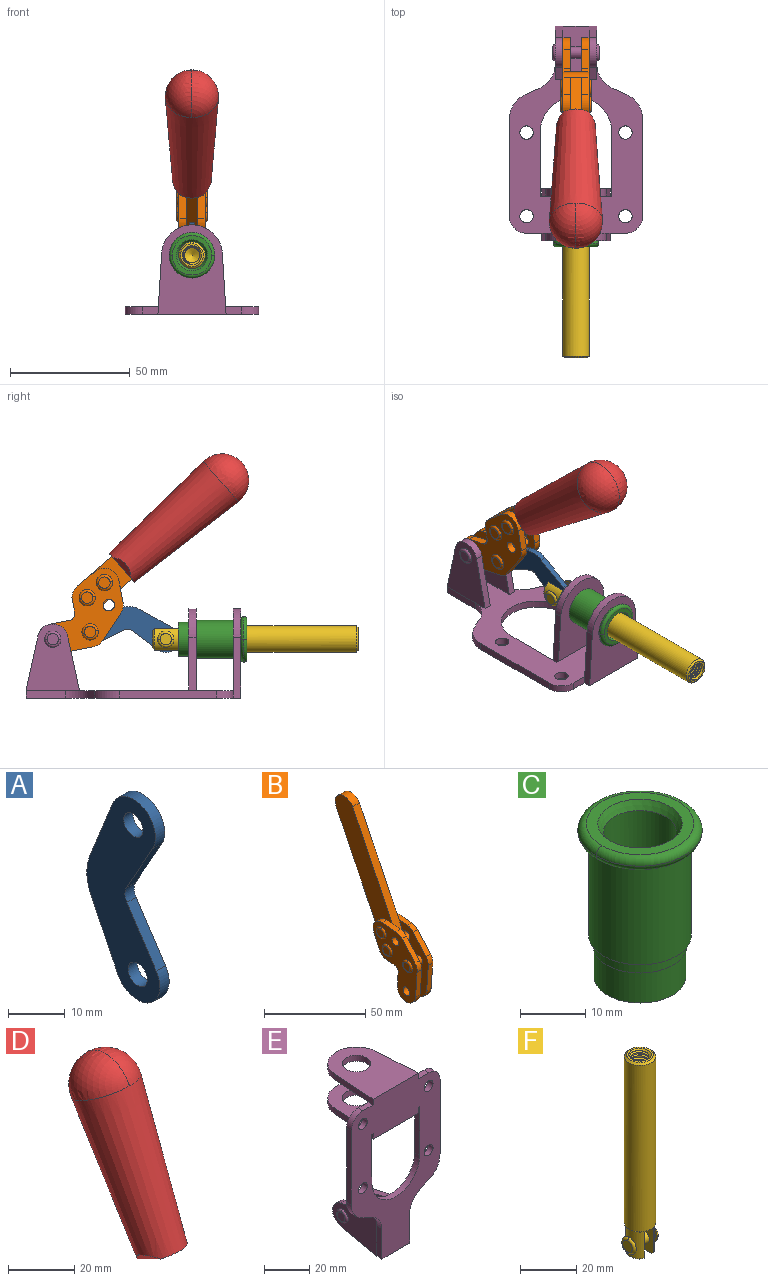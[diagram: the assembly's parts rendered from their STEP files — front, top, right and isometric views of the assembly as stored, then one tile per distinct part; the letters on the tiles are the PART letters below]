
ASSEMBLY  parts=6 mates=6
PART A: 12 faces, bbox 2.3x18.2x42.8 mm
  f0: cylinder r=2.4mm len=4.8mm, axis (1,0,0), area 34.9mm2, adj f4,f11
  f1: cylinder r=10.41mm len=8.47mm, axis (1,0,0), area 20.2mm2, adj f4,f9,f10,f11
  f2: cylinder r=3.05mm len=3.16mm, axis (1,0,0), area 7.7mm2, adj f4,f6,f7,f11
  f3: cylinder r=2.4mm len=4.8mm, axis (1,0,0), area 34.9mm2, adj f4,f11
  f4: plane 42.81x18.23mm, normal (-1,0,0), area 414.1mm2, adj f0,f1,f2,f3,f5,f6,f7,f8
  f5: cylinder r=5.54mm len=10.67mm, axis (1,0,0), area 41.8mm2, adj f4,f6,f10,f11
  f6: plane 11.66x6.53mm, normal (0,-0.87,-0.49), area 30.9mm2, adj f2,f4,f5,f11
  f7: plane 11.17x7.33mm, normal (0,-0.84,0.55), area 30.9mm2, adj f2,f4,f8,f11
  f8: cylinder r=5.54mm len=10.51mm, axis (1,0,0), area 41.8mm2, adj f4,f7,f9,f11
  f9: plane 13.67x6.67mm, normal (0,0.9,-0.44), area 35.1mm2, adj f1,f4,f8,f11
  f10: plane 14.1x5.7mm, normal (0,0.93,0.37), area 35.1mm2, adj f1,f4,f5,f11
  f11: plane 42.81x18.23mm, normal (1,0,0), area 414.1mm2, adj f0,f1,f2,f3,f5,f6,f7,f8
PART B: 59 faces, bbox 12.9x60.2x99.6 mm
  f0: torus R=2.39mm, axis (-1,0,0), area 14.9mm2, adj f20,f43,f51
  f1: torus R=2.39mm, axis (-1,0,0), area 14.9mm2, adj f19,f42,f51
  f2: torus R=2.39mm, axis (-1,0,0), area 14.9mm2, adj f18,f35,f51
  f3: torus R=2.39mm, axis (-1,0,0), area 14.9mm2, adj f14,f17,f23
  f4: torus R=2.39mm, axis (-1,0,0), area 14.9mm2, adj f13,f16,f23
  f5: torus R=2.39mm, axis (-1,0,0), area 14.9mm2, adj f12,f15,f23
  f6: cylinder r=2.39mm len=4.78mm, axis (1,0,0), area 46.5mm2, adj f48,f50,f51
  f7: cylinder r=2.39mm len=4.78mm, axis (1,0,0), area 46.5mm2, adj f50,f51
  f8: cylinder r=6.35mm len=12.68mm, axis (1,0,0), area 61.8mm2, adj f38,f39,f50,f51
  f9: cylinder r=2.39mm len=4.78mm, axis (-1,0,0), area 70.5mm2, adj f46,f50
  f10: cylinder r=2.39mm len=4.78mm, axis (-1,0,0), area 46.5mm2, adj f23,f45,f46
  f11: cylinder r=2.39mm len=4.78mm, axis (-1,0,0), area 46.5mm2, adj f23,f46
  f12: plane 4.78x4.78mm, normal (1,0,0), area 17.9mm2, adj f5,f15
  f13: plane 4.78x4.78mm, normal (1,0,0), area 17.9mm2, adj f4,f16
  f14: plane 4.78x4.78mm, normal (1,0,0), area 17.9mm2, adj f3,f17
  f15: torus R=2.39mm, axis (-1,0,0), area 14.9mm2, adj f5,f12,f23
  f16: torus R=2.39mm, axis (-1,0,0), area 14.9mm2, adj f4,f13,f23
  f17: torus R=2.39mm, axis (-1,0,0), area 14.9mm2, adj f3,f14,f23
  f18: plane 4.78x4.78mm, normal (-1,0,0), area 17.9mm2, adj f2,f35
  f19: plane 4.78x4.78mm, normal (-1,0,0), area 17.9mm2, adj f1,f42
  f20: plane 4.78x4.78mm, normal (-1,0,0), area 17.9mm2, adj f0,f43
  f21: plane 2.26x0.2mm, normal (1,0,0), area 0.2mm2, adj f31,f44
  f22: plane 2.26x0.2mm, normal (-1,0,0), area 0.2mm2, adj f41,f44
  f23: plane 39.37x30.77mm, normal (1,0,0), area 565.5mm2, adj f3,f4,f5,f10,f11,f15,f16,f17
  f24: cylinder r=6.1mm len=4.15mm, axis (-1,0,0), area 14.7mm2, adj f23,f25,f32,f46
  f25: plane 10.25x9.01mm, normal (0,-0.75,0.66), area 42.3mm2, adj f23,f24,f26,f46
  f26: cylinder r=6.35mm len=4.64mm, axis (-1,0,0), area 15.6mm2, adj f23,f25,f27,f46
  f27: plane 15.84x3.1mm, normal (0,-1,-0.07), area 49.2mm2, adj f23,f26,f28,f46
  f28: cylinder r=6.35mm len=12.68mm, axis (-1,0,0), area 61.8mm2, adj f23,f27,f29,f46
  f29: plane 8.11x3.1mm, normal (0,1,0.07), area 25.2mm2, adj f23,f28,f30,f46
  f30: cylinder r=3.05mm len=3.25mm, axis (-1,0,0), area 14.8mm2, adj f23,f29,f31,f46
  f31: plane 5.99x3.1mm, normal (0,0.07,-1), area 18.6mm2, adj f21,f23,f30,f44,f46
  f32: plane 9.5x3.1mm, normal (0,-0.07,1), area 29.5mm2, adj f23,f24,f33,f46,f47
  f33: cylinder r=6.1mm len=8.63mm, axis (-1,0,0), area 39.1mm2, adj f23,f32,f34,f47
  f34: plane 8.65x3.96mm, normal (0,0.91,-0.42), area 29.5mm2, adj f23,f33,f44,f47
  f35: torus R=2.39mm, axis (-1,0,0), area 14.9mm2, adj f2,f18,f51
  f36: plane 10.25x9.01mm, normal (0,-0.75,0.66), area 42.3mm2, adj f37,f49,f50,f51
  f37: cylinder r=6.35mm len=4.64mm, axis (1,0,0), area 15.6mm2, adj f36,f38,f50,f51
  f38: plane 15.84x3.1mm, normal (0,-1,-0.07), area 49.2mm2, adj f8,f37,f50,f51
  f39: plane 8.11x3.1mm, normal (0,1,0.07), area 25.2mm2, adj f8,f40,f50,f51
  f40: cylinder r=3.05mm len=3.25mm, axis (1,0,0), area 14.8mm2, adj f39,f41,f50,f51
  f41: plane 5.99x3.1mm, normal (0,0.07,-1), area 18.6mm2, adj f22,f40,f44,f50,f51
  f42: torus R=2.39mm, axis (-1,0,0), area 14.9mm2, adj f1,f19,f51
  f43: torus R=2.39mm, axis (-1,0,0), area 14.9mm2, adj f0,f20,f51
  f44: cylinder r=6.35mm len=12.12mm, axis (-1,0,0), area 128.9mm2, adj f21,f22,f23,f31,f34,f41,f46,f47
  f45: plane 2.65x1.35mm, normal (1,0,0), area 1mm2, adj f10,f55
  f46: plane 39.08x20.42mm, normal (-1,0,0), area 412.5mm2, adj f9,f10,f11,f24,f25,f26,f27,f28
  f47: plane 77.62x39.82mm, normal (1,0,0), area 850mm2, adj f32,f33,f34,f44,f53,f54,f55
  f48: plane 2.65x1.35mm, normal (-1,0,0), area 1mm2, adj f6,f55
  f49: cylinder r=6.1mm len=4.15mm, axis (1,0,0), area 14.7mm2, adj f36,f50,f51,f56
  f50: plane 39.08x20.42mm, normal (1,0,0), area 412.5mm2, adj f6,f7,f8,f9,f36,f37,f38,f39
  f51: plane 39.37x30.77mm, normal (-1,0,0), area 565.5mm2, adj f0,f1,f2,f6,f7,f8,f35,f36
  f52: plane 8.65x3.96mm, normal (0,0.91,-0.42), area 29.5mm2, adj f44,f51,f57,f58
  f53: plane 68.49x33.4mm, normal (0,0.9,-0.44), area 358.1mm2, adj f44,f47,f54,f58
  f54: cylinder r=6.35mm len=12.06mm, axis (1,0,0), area 93.7mm2, adj f47,f53,f55,f58
  f55: plane 68.49x33.4mm, normal (0,-0.9,0.44), area 358.1mm2, adj f44,f45,f46,f47,f48,f50,f54,f58
  f56: plane 9.5x3.1mm, normal (0,-0.07,1), area 29.5mm2, adj f49,f50,f51,f57,f58
  f57: cylinder r=6.1mm len=8.63mm, axis (1,0,0), area 39.1mm2, adj f51,f52,f56,f58
  f58: plane 77.62x39.82mm, normal (-1,0,0), area 850mm2, adj f44,f52,f53,f54,f55,f56,f57
PART C: 15 faces, bbox 20.6x20.6x28.7 mm
  f0: torus R=8.26mm, axis (0,0,1), area 56.8mm2, adj f1,f10,f12
  f1: torus R=8.26mm, axis (0,0,1), area 56.8mm2, adj f0,f6,f13
  f2: cylinder r=5.59mm len=25.91mm, axis (0,0,1), area 909.6mm2, adj f3,f4
  f3: cone r=6.86mm half-angle=45deg, axis (0,0,-1), area 70.2mm2, adj f2,f14
  f4: cone r=6.47mm half-angle=30deg, axis (0,0,1), area 66.7mm2, adj f2,f13
  f5: cylinder r=7.04mm len=14.07mm, axis (0,0,1), area 252.6mm2, adj f11,f14
  f6: torus R=8.26mm, axis (0,0,1), area 56.8mm2, adj f1,f12,f13
  f7: cylinder r=7.16mm len=14.33mm, axis (0,0,1), area 91.5mm2, adj f9,f11
  f8: cylinder r=7.86mm len=18.42mm, axis (0,0,1), area 909.6mm2, adj f9,f10
  f9: plane 15.72x15.72mm, normal (0,0,-1), area 33mm2, adj f7,f8
  f10: plane 16.51x16.51mm, normal (0,0,-1), area 19.9mm2, adj f0,f8,f12
  f11: plane 14.33x14.33mm, normal (0,0,-1), area 5.7mm2, adj f5,f7
  f12: torus R=8.26mm, axis (0,0,1), area 56.8mm2, adj f0,f6,f10
  f13: plane 16.51x16.51mm, normal (0,0,1), area 82.7mm2, adj f1,f4,f6
  f14: plane 14.07x14.07mm, normal (0,0,-1), area 7.8mm2, adj f3,f5
PART D: 11 faces, bbox 22.3x42.6x64.5 mm
  f0: sphere r=11.13mm, area 411.4mm2, adj f1,f8
  f1: cone r=11.11mm half-angle=3.3deg, axis (0,0.44,0.9), area 3251.8mm2, adj f0,f7,f8,f9,f10
  f2: cylinder r=6.16mm len=11.7mm, axis (1,0,0), area 89.5mm2, adj f3,f4,f5,f6
  f3: plane 60.23x36.75mm, normal (-1,0,0), area 763.6mm2, adj f2,f4,f6,f10
  f4: plane 51.37x25.05mm, normal (0,0.9,-0.44), area 264.2mm2, adj f2,f3,f5,f10
  f5: plane 60.23x36.75mm, normal (1,0,0), area 763.6mm2, adj f2,f4,f6,f10
  f6: plane 51.37x25.05mm, normal (0,-0.9,0.44), area 264.2mm2, adj f2,f3,f5,f10
  f7: plane 9.95x5.95mm, normal (0.71,-0.31,-0.64), area 25.8mm2, adj f1,f10
  f8: sphere r=11.13mm, area 411.4mm2, adj f0,f1
  f9: plane 9.95x5.95mm, normal (-0.71,-0.31,-0.64), area 25.8mm2, adj f1,f10
  f10: plane 14.27x11.38mm, normal (0,-0.44,-0.9), area 106.7mm2, adj f1,f3,f4,f5,f6,f7,f9
PART E: 55 faces, bbox 55.7x37.4x89.8 mm
  f0: torus R=2.41mm, axis (-1,0,0), area 15mm2, adj f11,f15,f25
  f1: torus R=2.41mm, axis (-1,0,0), area 15mm2, adj f10,f12,f22
  f2: cylinder r=2.78mm len=5.56mm, axis (0,-1,0), area 54.2mm2, adj f30,f54
  f3: cylinder r=14.99mm len=29.97mm, axis (0,-1,0), area 145.9mm2, adj f30,f49,f53,f54
  f4: cylinder r=2.78mm len=5.56mm, axis (0,-1,0), area 54.2mm2, adj f30,f54
  f5: cylinder r=2.78mm len=5.56mm, axis (0,-1,0), area 54.2mm2, adj f30,f54
  f6: cylinder r=2.78mm len=5.56mm, axis (0,-1,0), area 54.2mm2, adj f30,f54
  f7: cylinder r=6.35mm len=12.7mm, axis (0,0,1), area 123.6mm2, adj f27,f51
  f8: cylinder r=6.35mm len=12.7mm, axis (0,0,-1), area 124.7mm2, adj f21,f35
  f9: cylinder r=2.41mm len=11.18mm, axis (-1,0,0), area 169.4mm2, adj f16,f19
  f10: plane 4.83x4.83mm, normal (1,0,0), area 18.3mm2, adj f1,f12
  f11: plane 4.83x4.83mm, normal (-1,0,0), area 18.3mm2, adj f0,f15
  f12: torus R=2.41mm, axis (-1,0,0), area 15mm2, adj f1,f10,f22
  f13: cylinder r=6.35mm len=12.41mm, axis (1,0,0), area 53.4mm2, adj f18,f19,f22,f23
  f14: cylinder r=6.35mm len=12.41mm, axis (-1,0,0), area 53.4mm2, adj f16,f17,f24,f25
  f15: torus R=2.41mm, axis (-1,0,0), area 15mm2, adj f0,f11,f25
  f16: plane 27.86x22.35mm, normal (1,0,0), area 425.4mm2, adj f9,f14,f17,f24,f30
  f17: plane 22.86x4.97mm, normal (0,0.21,0.98), area 72.5mm2, adj f14,f16,f25,f30
  f18: plane 22.86x4.97mm, normal (0,0.21,0.98), area 72.5mm2, adj f13,f19,f22,f30
  f19: plane 27.86x22.35mm, normal (-1,0,0), area 425.4mm2, adj f9,f13,f18,f23,f30
  f20: cylinder r=12.7mm len=25.35mm, axis (0,0,-1), area 119.8mm2, adj f21,f34,f35,f36
  f21: plane 34.21x28.07mm, normal (0,0,-1), area 702.4mm2, adj f8,f20,f30,f34,f36
  f22: plane 27.96x22.45mm, normal (1,0,0), area 407.2mm2, adj f1,f12,f13,f18,f23,f30,f42,f43
  f23: plane 22.86x4.97mm, normal (0,0.21,-0.98), area 72.5mm2, adj f13,f19,f22,f44
  f24: plane 22.86x4.97mm, normal (0,0.21,-0.98), area 72.5mm2, adj f14,f16,f25,f44
  f25: plane 27.86x22.35mm, normal (-1,0,0), area 407.1mm2, adj f0,f14,f15,f17,f24,f30,f45,f46
  f26: plane 3.1x0.95mm, normal (0,0,-1), area 2.7mm2, adj f30,f49,f50,f54
  f27: plane 34.21x28.07mm, normal (0,0,1), area 702.4mm2, adj f7,f28,f30,f50,f52
  f28: cylinder r=12.7mm len=25.35mm, axis (0,0,1), area 118.8mm2, adj f27,f50,f51,f52
  f29: plane 3.1x0.95mm, normal (0,0,-1), area 2.7mm2, adj f30,f52,f53,f54
  f30: plane 86.54x55.63mm, normal (0,1,0), area 2362.9mm2, adj f2,f3,f4,f5,f6,f16,f17,f18
  f31: plane 40.56x3.1mm, normal (-1,0,0), area 125.7mm2, adj f30,f32,f48,f54
  f32: cylinder r=7.11mm len=7.11mm, axis (0,-1,0), area 34.6mm2, adj f30,f31,f33,f54
  f33: plane 6.67x3.1mm, normal (0,0,1), area 20.4mm2, adj f30,f32,f34,f54
  f34: plane 25.39x3.13mm, normal (-1,0.06,0), area 79.5mm2, adj f20,f21,f33,f35,f54
  f35: plane 37.31x28.45mm, normal (0,0,1), area 789.9mm2, adj f8,f20,f34,f36,f54
  f36: plane 25.39x3.13mm, normal (1,0.06,0), area 79.5mm2, adj f20,f21,f35,f37,f54
  f37: plane 6.67x3.1mm, normal (0,0,1), area 20.4mm2, adj f30,f36,f38,f54
  f38: cylinder r=7.11mm len=7.11mm, axis (0,-1,0), area 34.6mm2, adj f30,f37,f39,f54
  f39: plane 40.56x3.1mm, normal (1,0,0), area 125.7mm2, adj f30,f38,f40,f54
  f40: cylinder r=11.18mm len=10.16mm, axis (0,-1,0), area 39.5mm2, adj f30,f39,f41,f54
  f41: plane 6.09x3.1mm, normal (0.42,0,-0.91), area 20.8mm2, adj f30,f40,f42,f54
  f42: cylinder r=11.18mm len=9.41mm, axis (0,-1,0), area 37.2mm2, adj f22,f30,f41,f43,f54
  f43: plane 16.5x3.1mm, normal (1,0,0), area 51.1mm2, adj f22,f42,f44,f54
  f44: plane 17.37x3.1mm, normal (0,0,-1), area 53.8mm2, adj f23,f24,f30,f43,f45,f54
  f45: plane 16.5x3.1mm, normal (-1,0,0), area 51.1mm2, adj f25,f44,f46,f54
  f46: cylinder r=11.18mm len=9.41mm, axis (0,-1,0), area 37.2mm2, adj f25,f30,f45,f47,f54
  f47: plane 6.09x3.1mm, normal (-0.42,0,-0.91), area 20.8mm2, adj f30,f46,f48,f54
  f48: cylinder r=11.18mm len=10.16mm, axis (0,-1,0), area 39.5mm2, adj f30,f31,f47,f54
  f49: plane 26.54x3.1mm, normal (-1,0,0), area 82.3mm2, adj f3,f26,f30,f54
  f50: plane 25.39x3.1mm, normal (1,0.06,0), area 78.8mm2, adj f26,f27,f28,f51,f54
  f51: plane 37.31x28.45mm, normal (0,0,-1), area 789.9mm2, adj f7,f28,f50,f52,f54
  f52: plane 25.39x3.1mm, normal (-1,0.06,0), area 78.8mm2, adj f27,f28,f29,f51,f54
  f53: plane 26.54x3.1mm, normal (1,0,0), area 82.3mm2, adj f3,f29,f30,f54
  f54: plane 89.66x55.63mm, normal (0,-1,0), area 2678.5mm2, adj f2,f3,f4,f5,f6,f26,f29,f31
PART F: 48 faces, bbox 12.6x11.1x86.1 mm
  f0: torus R=2.41mm, axis (-1,0,0), area 15mm2, adj f30,f32,f34
  f1: torus R=2.41mm, axis (-1,0,0), area 15mm2, adj f29,f31,f33
  f2: cylinder r=5.54mm len=72.39mm, axis (0,0,1), area 2518.5mm2, adj f3,f4,f42,f43
  f3: cone r=5.54mm half-angle=45deg, axis (0,0,1), area 7.6mm2, adj f2,f5,f41
  f4: cone r=5.54mm half-angle=45deg, axis (0,0,-1), area 34.9mm2, adj f2,f39
  f5: cylinder r=5.08mm len=11.48mm, axis (0,0,1), area 108.3mm2, adj f3,f7,f8,f41
  f6: cylinder r=2.41mm len=4.83mm, axis (-1,0,0), area 71.2mm2, adj f40,f41
  f7: cylinder r=2.41mm len=4.83mm, axis (-1,0,0), area 7.6mm2, adj f5,f34
  f8: cone r=5.08mm half-angle=45deg, axis (0,0,1), area 10.6mm2, adj f5,f37,f41
  f9: cone r=3.98mm half-angle=45deg, axis (0,0,1), area 17.6mm2, adj f27,f39,f45,f46,f47
  f10: cylinder r=2.41mm len=4.83mm, axis (-1,0,0), area 7.6mm2, adj f33,f38
  f11: cylinder r=3.2mm len=6.4mm, axis (0,0,1), area 78.4mm2, adj f12,f28,f44,f45,f47
  f12: cylinder r=3.2mm len=6.4mm, axis (0,0,1), area 10.5mm2, adj f11,f13,f45,f47
  f13: cylinder r=3.2mm len=6.4mm, axis (0,0,1), area 10.5mm2, adj f12,f14,f45,f47
  f14: cylinder r=3.2mm len=6.4mm, axis (0,0,1), area 10.5mm2, adj f13,f15,f45,f47
  f15: cylinder r=3.2mm len=6.4mm, axis (0,0,1), area 10.5mm2, adj f14,f16,f45,f47
  f16: cylinder r=3.2mm len=6.4mm, axis (0,0,1), area 10.5mm2, adj f15,f17,f45,f47
  f17: cylinder r=3.2mm len=6.4mm, axis (0,0,1), area 10.5mm2, adj f16,f18,f45,f47
  f18: cylinder r=3.2mm len=6.4mm, axis (0,0,1), area 10.5mm2, adj f17,f19,f45,f47
  f19: cylinder r=3.2mm len=6.4mm, axis (0,0,1), area 10.5mm2, adj f18,f20,f45,f47
  f20: cylinder r=3.2mm len=6.4mm, axis (0,0,1), area 10.5mm2, adj f19,f21,f45,f47
  f21: cylinder r=3.2mm len=6.4mm, axis (0,0,1), area 10.5mm2, adj f20,f22,f45,f47
  f22: cylinder r=3.2mm len=6.4mm, axis (0,0,1), area 10.5mm2, adj f21,f23,f45,f47
  f23: cylinder r=3.2mm len=6.4mm, axis (0,0,1), area 10.5mm2, adj f22,f24,f45,f47
  f24: cylinder r=3.2mm len=6.4mm, axis (0,0,1), area 10.5mm2, adj f23,f25,f45,f47
  f25: cylinder r=3.2mm len=6.4mm, axis (0,0,1), area 10.5mm2, adj f24,f26,f45,f47
  f26: cylinder r=3.2mm len=6.4mm, axis (0,0,1), area 10.5mm2, adj f25,f27,f45,f47
  f27: cylinder r=3.2mm len=6.4mm, axis (0,0,1), area 7.4mm2, adj f9,f26,f45,f47
  f28: cone r=3.2mm half-angle=60deg, axis (0,0,1), area 37.2mm2, adj f11
  f29: plane 4.83x4.83mm, normal (-1,0,0), area 18.3mm2, adj f1,f31
  f30: plane 4.83x4.83mm, normal (1,0,0), area 18.3mm2, adj f0,f32
  f31: torus R=2.41mm, axis (-1,0,0), area 15mm2, adj f1,f29,f33
  f32: torus R=2.41mm, axis (-1,0,0), area 15mm2, adj f0,f30,f34
  f33: plane 6.83x6.83mm, normal (1,0,0), area 18.3mm2, adj f1,f10,f31
  f34: plane 6.83x6.83mm, normal (-1,0,0), area 18.3mm2, adj f0,f7,f32
  f35: cone r=5.08mm half-angle=45deg, axis (0,0,1), area 10.6mm2, adj f36,f38,f40
  f36: plane 7.25x1.97mm, normal (0,0,-1), area 10mm2, adj f35,f40
  f37: plane 7.25x1.97mm, normal (0,0,-1), area 10mm2, adj f8,f41
  f38: cylinder r=5.08mm len=11.48mm, axis (0,0,1), area 108.3mm2, adj f10,f35,f40,f42
  f39: plane 9.55x9.55mm, normal (0,0,1), area 22mm2, adj f4,f9
  f40: plane 12.76x10.09mm, normal (1,0,0), area 95.7mm2, adj f6,f35,f36,f38,f42,f43
  f41: plane 12.76x10.09mm, normal (-1,0,0), area 95.7mm2, adj f3,f5,f6,f8,f37,f43
  f42: cone r=5.54mm half-angle=45deg, axis (0,0,1), area 7.6mm2, adj f2,f38,f40
  f43: plane 11.07x4.7mm, normal (0,0,-1), area 50.4mm2, adj f2,f40,f41
  f44: plane 0.89x0.62mm, normal (-1,0,0), area 0.3mm2, adj f11,f45,f46,f47
  f45: bspline ~24.8x7.63mm, area 266.6mm2, adj f9,f11,f12,f13,f14,f15,f16,f17
  f46: bspline ~24.87x7.63mm, area 73.6mm2, adj f9,f44,f45,f47
  f47: bspline ~24.98x7.63mm, area 272.5mm2, adj f9,f11,f12,f13,f14,f15,f16,f17
PLACE A rot(axis=(0,-0.69,-0.73),180deg) t=(0,11.99,2.14)mm
PLACE B rot(axis=(1,0,0),75deg) t=(0,4.15,9.14)mm
PLACE C rot(axis=(1,0,0),90deg) t=(0,9.43,0)mm
PLACE D rot(axis=(1,0,0),75deg) t=(-0.04,4.15,9.14)mm
PLACE E rot(axis=(1,0,0),90deg) t=(0,9.43,0)mm fixed
PLACE F rot(axis=(1,0,0),90deg) t=(0,9.81,0)mm
MATE fastened C.f2 <-> E.f7  axis (0,1,0) through (0,-36.96,24.61)mm
MATE revolute A.f5 <-> B.f4  axis (-1,0,0) through (0,25.94,27.64)mm
MATE revolute A.f3 <-> F.f6  axis (-1,0,0) through (0,-5.67,24.61)mm
MATE slider E.f7 <-> F.f2  axis (0,-1,0) through (0,-36.96,24.61)mm
MATE revolute B.f7 <-> E.f0  axis (1,0,0) through (0,41.52,24.61)mm
MATE fastened D.f2 <-> B.f54  axis (1,0,0) through (-2.35,-30.37,91.94)mm
